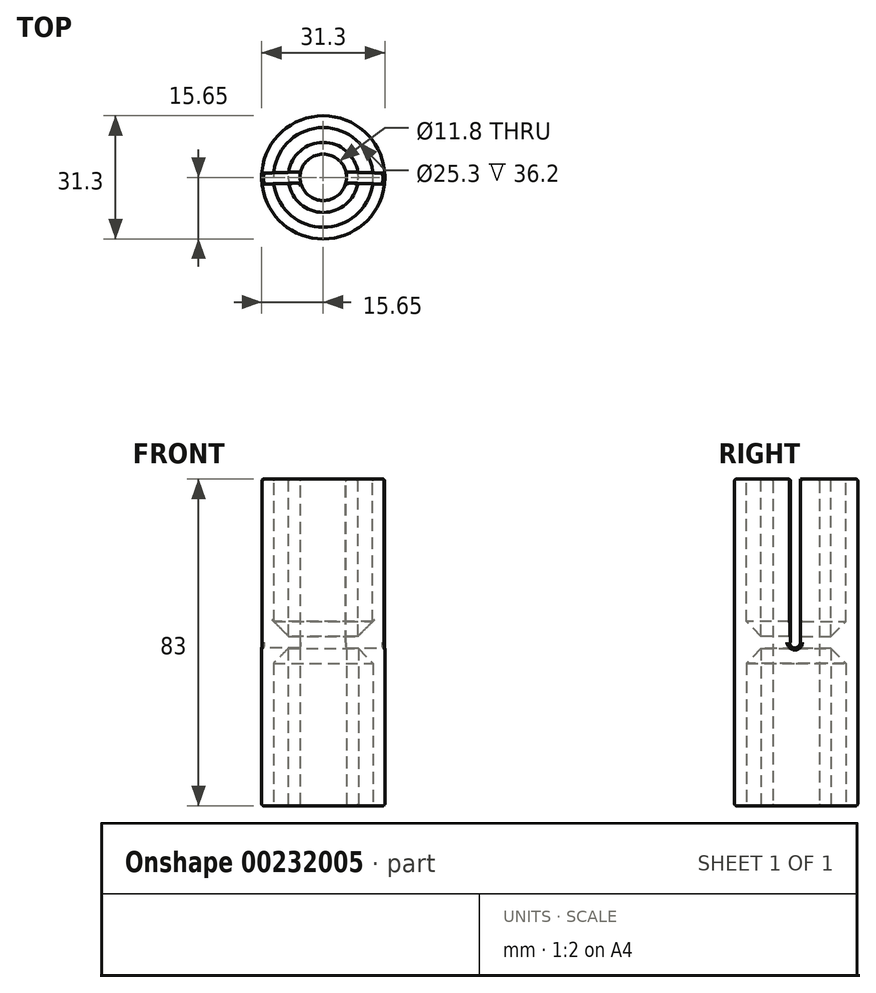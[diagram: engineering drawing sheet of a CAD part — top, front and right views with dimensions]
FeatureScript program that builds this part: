
annotation { "Feature Type Name" : "Feature", "Feature Type Description" : "" }
export const myFeature = defineFeature(function(context is Context, id is Id, definition is map)
    precondition{}
    {
        {
            var Q0;
            Q0=qCreatedBy(makeId("Top.planeOp"),FACE);
            var sketch = newSketch(context, id + "F0", { "sketchPlane" : qUnion([Q0])});
            skCircle(sketch, "E0", {"center": v(0, 0) * mm, "radius": 15.65 * mm});
            skCircle(sketch, "E1", {"center": v(0, 0) * mm, "radius": 5.9 * mm});
            skSolve(sketch);
        }
        {
            var Q0;
            Q0 = qSketchRegion(id + "F0", true);
            extrude(context, id + "F1", {"entities" : qUnion([Q0]), "endBound" : BoundingType.SYMMETRIC, "depth" : 83 * mm});
        }
        {
            var Q0;
            Q0=makeQuery(id+"F1.opExtrude","CAP_FACE",FACE,{"disambiguationData":[OSD([sQuery(id+"F0.wireOp",EDGE,"E0"),sQuery(id+"F0.wireOp",EDGE,"E1")])],"isStart":false});
            var sketch = newSketch(context, id + "F2", { "sketchPlane" : qUnion([Q0])});
            skCircle(sketch, "E2", {"center": v(0, 0) * mm, "radius": 12.65 * mm});
            skCircle(sketch, "E3", {"center": v(0, 0) * mm, "radius": 8.9 * mm});
            skSolve(sketch);
        }
        {
            var Q0;
            Q0 = qSketchRegion(id + "F2", true);
            extrude(context, id + "F3", {"entities" : qUnion([Q0]), "operationType" : NewBodyOperationType.REMOVE, "oppositeDirection" : true, "depth" : 40 * mm});
        }
        {
            var Q0;
            Q0=makeQuery(id+"F1.opExtrude","CAP_FACE",FACE,{"disambiguationData":[OSD([sQuery(id+"F0.wireOp",EDGE,"E0"),sQuery(id+"F0.wireOp",EDGE,"E1")])],"isStart":true});
            var sketch = newSketch(context, id + "F4", { "sketchPlane" : qUnion([Q0])});
            skCircle(sketch, "E4", {"center": v(0, 0) * mm, "radius": 8.9 * mm});
            skCircle(sketch, "E5", {"center": v(0, 0) * mm, "radius": 12.65 * mm});
            skSolve(sketch);
        }
        {
            var Q0;
            Q0 = qSketchRegion(id + "F4", true);
            extrude(context, id + "F5", {"entities" : qUnion([Q0]), "operationType" : NewBodyOperationType.REMOVE, "oppositeDirection" : true, "depth" : 40 * mm});
        }
        {
            var Q0;
            {var subQ0=sQuery(id+"F0.wireOp",EDGE,"E1");Q0=makeQuery(id+"F3.boolean.opBoolean","SPLIT",FACE,{"disambiguationData":[TD([makeQuery(id+"F1.opExtrude","SWEPT_FACE",FACE,{"disambiguationData":[OSD([subQ0])]})])],"derivedFrom":makeQuery(id+"F1.opExtrude","CAP_FACE",FACE,{"disambiguationData":[OSD([sQuery(id+"F0.wireOp",EDGE,"E0"),subQ0])],"isStart":false})});}
            var sketch = newSketch(context, id + "F6", { "sketchPlane" : qUnion([Q0])});
            skCircle(sketch, "E6", {"center": v(0, -340) * mm, "radius": 340 * mm, "construction": true});
            skPoint(sketch, "E7", {"position": v(0, 0) * mm});
            skSolve(sketch);
        }
        {
            var Q0;
            Q0=qCreatedBy(makeId("Right.planeOp"),FACE);
            var sketch = newSketch(context, id + "F7", { "sketchPlane" : qUnion([Q0])});
            skLineSegment(sketch, "E8", {"start": v(1.4, 41.5) * mm, "end": v(0, 41.5) * mm});
            skLineSegment(sketch, "E9", {"start": v(1.4, 41.5) * mm, "end": v(1.4, 0) * mm});
            skArc(sketch, "E10", {"start": v(0, -1.4) * mm, "mid": v(0.99, -0.99) * mm, "end": v(1.4, 0) * mm});
            skArc(sketch, "E11.MirrorCS", {"start": v(0, -1.4) * mm, "mid": v(-0.99, -0.99) * mm, "end": v(-1.4, 0) * mm});
            skLineSegment(sketch, "E12.MirrorCS", {"start": v(-1.4, 41.5) * mm, "end": v(-1.4, 0) * mm});
            skLineSegment(sketch, "E13", {"start": v(0, 41.5) * mm, "end": v(-1.4, 41.5) * mm});
            skSolve(sketch);
        }
        {
            var Q0;
            Q0=qCreatedBy(makeId("Right.planeOp"),FACE);
            var sketch = newSketch(context, id + "F8", { "sketchPlane" : qUnion([Q0])});
            skLineSegment(sketch, "E14", {"start": v(-340, -124.57) * mm, "end": v(-340, 184) * mm, "construction": true});
            skSolve(sketch);
        }
        {
            var Q0;
            Q0 = qSketchRegion(id + "F7", true);
            var Q1;
            Q1=sQuery(id+"F8.wireOp",EDGE,"E14");
            revolve(context, id + "F9", {"operationType" : NewBodyOperationType.REMOVE, "entities" : qUnion([Q0]), "axis" : qUnion([Q1]), "revolveType" : RevolveType.FULL, "oppositeDirection" : true});
        }
        {
            var Q0;
            Q0=makeQuery(id+"F5.boolean.opBoolean","COPY",EDGE,{"derivedFrom":makeQuery(id+"F5.opExtrude","CAP_EDGE",EDGE,{"disambiguationData":[OSD([sQuery(id+"F4.wireOp",EDGE,"E5")])],"isStart":false})});
            chamfer(context, id + "F10", {"entities" : qUnion([Q0]), "width" : 3.8 * mm, "tangentPropagation" : true});
        }
        {
            var Q0;
            {var subQ0=sQuery(id+"F2.wireOp",EDGE,"E2");Q0=makeQuery(id+"F9.boolean.opBoolean","SPLIT",EDGE,{"disambiguationData":[TD([makeQuery(id+"F9.opRevolve","SWEPT_FACE",FACE,{"disambiguationData":[OSD([sQuery(id+"F7.wireOp",EDGE,"E12.MirrorCS")])]})])],"derivedFrom":makeQuery(id+"F3.boolean.opBoolean","COPY",EDGE,{"derivedFrom":makeQuery(id+"F3.opExtrude","CAP_EDGE",EDGE,{"disambiguationData":[OSD([subQ0])],"isStart":false})})});}
            var Q1;
            {var subQ0=sQuery(id+"F2.wireOp",EDGE,"E2");Q1=makeQuery(id+"F9.boolean.opBoolean","SPLIT",EDGE,{"disambiguationData":[TD([makeQuery(id+"F9.opRevolve","SWEPT_FACE",FACE,{"disambiguationData":[OSD([sQuery(id+"F7.wireOp",EDGE,"E9")])]})])],"derivedFrom":makeQuery(id+"F3.boolean.opBoolean","COPY",EDGE,{"derivedFrom":makeQuery(id+"F3.opExtrude","CAP_EDGE",EDGE,{"disambiguationData":[OSD([subQ0])],"isStart":false})})});}
            chamfer(context, id + "F11", {"entities" : qUnion([Q0, Q1]), "width" : 3.8 * mm, "tangentPropagation" : true});
        }
        {
            var Q0;
            {var subQ0=sQuery(id+"F0.wireOp",EDGE,"E0");Q0=makeQuery(id+"F9.boolean.opBoolean","SPLIT",EDGE,{"disambiguationData":[TD([makeQuery(id+"F9.opRevolve","SWEPT_FACE",FACE,{"disambiguationData":[OSD([sQuery(id+"F7.wireOp",EDGE,"E9")])]})])],"derivedFrom":makeQuery(id+"F1.opExtrude","CAP_EDGE",EDGE,{"disambiguationData":[OSD([subQ0])],"isStart":false})});}
            var Q1;
            {var subQ0=sQuery(id+"F2.wireOp",EDGE,"E2");Q1=makeQuery(id+"F9.boolean.opBoolean","SPLIT",EDGE,{"disambiguationData":[TD([makeQuery(id+"F9.opRevolve","SWEPT_FACE",FACE,{"disambiguationData":[OSD([sQuery(id+"F7.wireOp",EDGE,"E9")])]})])],"derivedFrom":makeQuery(id+"F3.boolean.opBoolean","COPY",EDGE,{"derivedFrom":makeQuery(id+"F3.opExtrude","CAP_EDGE",EDGE,{"disambiguationData":[OSD([subQ0])],"isStart":true})})});}
            var Q2;
            Q2=makeQuery(id+"F9.boolean.opBoolean","INTERSECT",EDGE,{"disambiguationData":[OD(0.0)],"derivedFrom":[makeQuery(id+"F1.opExtrude","SWEPT_FACE",FACE,{"disambiguationData":[OSD([sQuery(id+"F0.wireOp",EDGE,"E0")])]}),makeQuery(id+"F9.opRevolve","SWEPT_FACE",FACE,{"disambiguationData":[OSD([sQuery(id+"F7.wireOp",EDGE,"E9")])]})]});
            var Q3;
            {var subQ0=sQuery(id+"F0.wireOp",EDGE,"E0");var subQ1=sQuery(id+"F7.wireOp",EDGE,"E9");Q3=makeQuery(id+"F9.boolean.opBoolean","COPY",EDGE,{"disambiguationData":[TD([makeQuery(id+"F1.opExtrude","SWEPT_FACE",FACE,{"disambiguationData":[OSD([subQ0])]}),makeQuery(id+"F1.opExtrude","CAP_FACE",FACE,{"disambiguationData":[OSD([subQ0,sQuery(id+"F0.wireOp",EDGE,"E1")])],"isStart":false}),makeQuery(id+"F3.boolean.opBoolean","COPY",FACE,{"derivedFrom":makeQuery(id+"F3.opExtrude","SWEPT_FACE",FACE,{"disambiguationData":[OSD([sQuery(id+"F2.wireOp",EDGE,"E2")])]})}),makeQuery(id+"F9.opRevolve","SWEPT_FACE",FACE,{"disambiguationData":[OSD([subQ1])]})]),OD(0.0)],"derivedFrom":makeQuery(id+"F9.opRevolve","SWEPT_EDGE",EDGE,{"disambiguationData":[OSD([sQuery(id+"F7.wireOp",EDGE,"E8"),subQ1])]})});}
            var Q4;
            {var subQ0=sQuery(id+"F0.wireOp",EDGE,"E0");var subQ1=sQuery(id+"F7.wireOp",EDGE,"E12.MirrorCS");Q4=makeQuery(id+"F9.boolean.opBoolean","COPY",EDGE,{"disambiguationData":[TD([makeQuery(id+"F1.opExtrude","SWEPT_FACE",FACE,{"disambiguationData":[OSD([subQ0])]}),makeQuery(id+"F1.opExtrude","CAP_FACE",FACE,{"disambiguationData":[OSD([subQ0,sQuery(id+"F0.wireOp",EDGE,"E1")])],"isStart":false}),makeQuery(id+"F3.boolean.opBoolean","COPY",FACE,{"derivedFrom":makeQuery(id+"F3.opExtrude","SWEPT_FACE",FACE,{"disambiguationData":[OSD([sQuery(id+"F2.wireOp",EDGE,"E2")])]})}),makeQuery(id+"F9.opRevolve","SWEPT_FACE",FACE,{"disambiguationData":[OSD([subQ1])]})]),OD(0.0)],"derivedFrom":makeQuery(id+"F9.opRevolve","SWEPT_EDGE",EDGE,{"disambiguationData":[OSD([subQ1,sQuery(id+"F7.wireOp",EDGE,"E13")])]})});}
            var Q5;
            {var subQ0=sQuery(id+"F0.wireOp",EDGE,"E0");Q5=makeQuery(id+"F9.boolean.opBoolean","SPLIT",EDGE,{"disambiguationData":[TD([makeQuery(id+"F9.opRevolve","SWEPT_FACE",FACE,{"disambiguationData":[OSD([sQuery(id+"F7.wireOp",EDGE,"E12.MirrorCS")])]})])],"derivedFrom":makeQuery(id+"F1.opExtrude","CAP_EDGE",EDGE,{"disambiguationData":[OSD([subQ0])],"isStart":false})});}
            var Q6;
            {var subQ0=sQuery(id+"F2.wireOp",EDGE,"E2");Q6=makeQuery(id+"F9.boolean.opBoolean","SPLIT",EDGE,{"disambiguationData":[TD([makeQuery(id+"F9.opRevolve","SWEPT_FACE",FACE,{"disambiguationData":[OSD([sQuery(id+"F7.wireOp",EDGE,"E12.MirrorCS")])]})])],"derivedFrom":makeQuery(id+"F3.boolean.opBoolean","COPY",EDGE,{"derivedFrom":makeQuery(id+"F3.opExtrude","CAP_EDGE",EDGE,{"disambiguationData":[OSD([subQ0])],"isStart":true})})});}
            var Q7;
            Q7=makeQuery(id+"F9.boolean.opBoolean","INTERSECT",EDGE,{"disambiguationData":[OD(0.0)],"derivedFrom":[makeQuery(id+"F3.boolean.opBoolean","COPY",FACE,{"derivedFrom":makeQuery(id+"F3.opExtrude","SWEPT_FACE",FACE,{"disambiguationData":[OSD([sQuery(id+"F2.wireOp",EDGE,"E2")])]})}),makeQuery(id+"F9.opRevolve","SWEPT_FACE",FACE,{"disambiguationData":[OSD([sQuery(id+"F7.wireOp",EDGE,"E9")])]})]});
            var Q8;
            Q8=makeQuery(id+"F9.boolean.opBoolean","INTERSECT",EDGE,{"disambiguationData":[OD(1.0)],"derivedFrom":[makeQuery(id+"F1.opExtrude","SWEPT_FACE",FACE,{"disambiguationData":[OSD([sQuery(id+"F0.wireOp",EDGE,"E0")])]}),makeQuery(id+"F9.opRevolve","SWEPT_FACE",FACE,{"disambiguationData":[OSD([sQuery(id+"F7.wireOp",EDGE,"E9")])]})]});
            var Q9;
            Q9=makeQuery(id+"F9.boolean.opBoolean","INTERSECT",EDGE,{"disambiguationData":[OD(1.0)],"derivedFrom":[makeQuery(id+"F3.boolean.opBoolean","COPY",FACE,{"derivedFrom":makeQuery(id+"F3.opExtrude","SWEPT_FACE",FACE,{"disambiguationData":[OSD([sQuery(id+"F2.wireOp",EDGE,"E2")])]})}),makeQuery(id+"F9.opRevolve","SWEPT_FACE",FACE,{"disambiguationData":[OSD([sQuery(id+"F7.wireOp",EDGE,"E9")])]})]});
            var Q10;
            {var subQ0=sQuery(id+"F0.wireOp",EDGE,"E0");var subQ1=sQuery(id+"F7.wireOp",EDGE,"E9");Q10=makeQuery(id+"F9.boolean.opBoolean","COPY",EDGE,{"disambiguationData":[TD([makeQuery(id+"F1.opExtrude","SWEPT_FACE",FACE,{"disambiguationData":[OSD([subQ0])]}),makeQuery(id+"F1.opExtrude","CAP_FACE",FACE,{"disambiguationData":[OSD([subQ0,sQuery(id+"F0.wireOp",EDGE,"E1")])],"isStart":false}),makeQuery(id+"F3.boolean.opBoolean","COPY",FACE,{"derivedFrom":makeQuery(id+"F3.opExtrude","SWEPT_FACE",FACE,{"disambiguationData":[OSD([sQuery(id+"F2.wireOp",EDGE,"E2")])]})}),makeQuery(id+"F9.opRevolve","SWEPT_FACE",FACE,{"disambiguationData":[OSD([subQ1])]})]),OD(1.0)],"derivedFrom":makeQuery(id+"F9.opRevolve","SWEPT_EDGE",EDGE,{"disambiguationData":[OSD([sQuery(id+"F7.wireOp",EDGE,"E8"),subQ1])]})});}
            var Q11;
            {var subQ0=sQuery(id+"F0.wireOp",EDGE,"E0");var subQ1=sQuery(id+"F7.wireOp",EDGE,"E12.MirrorCS");Q11=makeQuery(id+"F9.boolean.opBoolean","COPY",EDGE,{"disambiguationData":[TD([makeQuery(id+"F1.opExtrude","SWEPT_FACE",FACE,{"disambiguationData":[OSD([subQ0])]}),makeQuery(id+"F1.opExtrude","CAP_FACE",FACE,{"disambiguationData":[OSD([subQ0,sQuery(id+"F0.wireOp",EDGE,"E1")])],"isStart":false}),makeQuery(id+"F3.boolean.opBoolean","COPY",FACE,{"derivedFrom":makeQuery(id+"F3.opExtrude","SWEPT_FACE",FACE,{"disambiguationData":[OSD([sQuery(id+"F2.wireOp",EDGE,"E2")])]})}),makeQuery(id+"F9.opRevolve","SWEPT_FACE",FACE,{"disambiguationData":[OSD([subQ1])]})]),OD(1.0)],"derivedFrom":makeQuery(id+"F9.opRevolve","SWEPT_EDGE",EDGE,{"disambiguationData":[OSD([subQ1,sQuery(id+"F7.wireOp",EDGE,"E13")])]})});}
            var Q12;
            {var subQ0=sQuery(id+"F2.wireOp",EDGE,"E3");Q12=makeQuery(id+"F9.boolean.opBoolean","SPLIT",EDGE,{"disambiguationData":[TD([makeQuery(id+"F9.opRevolve","SWEPT_FACE",FACE,{"disambiguationData":[OSD([sQuery(id+"F7.wireOp",EDGE,"E12.MirrorCS")])]})])],"derivedFrom":makeQuery(id+"F3.boolean.opBoolean","COPY",EDGE,{"derivedFrom":makeQuery(id+"F3.opExtrude","CAP_EDGE",EDGE,{"disambiguationData":[OSD([subQ0])],"isStart":true})})});}
            var Q13;
            {var subQ0=sQuery(id+"F0.wireOp",EDGE,"E1");var subQ1=sQuery(id+"F7.wireOp",EDGE,"E12.MirrorCS");Q13=makeQuery(id+"F9.boolean.opBoolean","COPY",EDGE,{"disambiguationData":[TD([makeQuery(id+"F1.opExtrude","CAP_FACE",FACE,{"disambiguationData":[OSD([sQuery(id+"F0.wireOp",EDGE,"E0"),subQ0])],"isStart":false}),makeQuery(id+"F1.opExtrude","SWEPT_FACE",FACE,{"disambiguationData":[OSD([subQ0])]}),makeQuery(id+"F3.boolean.opBoolean","COPY",FACE,{"derivedFrom":makeQuery(id+"F3.opExtrude","SWEPT_FACE",FACE,{"disambiguationData":[OSD([sQuery(id+"F2.wireOp",EDGE,"E3")])]})}),makeQuery(id+"F9.opRevolve","SWEPT_FACE",FACE,{"disambiguationData":[OSD([subQ1])]})]),OD(1.0)],"derivedFrom":makeQuery(id+"F9.opRevolve","SWEPT_EDGE",EDGE,{"disambiguationData":[OSD([subQ1,sQuery(id+"F7.wireOp",EDGE,"E13")])]})});}
            var Q14;
            {var subQ0=sQuery(id+"F0.wireOp",EDGE,"E1");var subQ1=sQuery(id+"F7.wireOp",EDGE,"E9");Q14=makeQuery(id+"F9.boolean.opBoolean","COPY",EDGE,{"disambiguationData":[TD([makeQuery(id+"F1.opExtrude","CAP_FACE",FACE,{"disambiguationData":[OSD([sQuery(id+"F0.wireOp",EDGE,"E0"),subQ0])],"isStart":false}),makeQuery(id+"F1.opExtrude","SWEPT_FACE",FACE,{"disambiguationData":[OSD([subQ0])]}),makeQuery(id+"F3.boolean.opBoolean","COPY",FACE,{"derivedFrom":makeQuery(id+"F3.opExtrude","SWEPT_FACE",FACE,{"disambiguationData":[OSD([sQuery(id+"F2.wireOp",EDGE,"E3")])]})}),makeQuery(id+"F9.opRevolve","SWEPT_FACE",FACE,{"disambiguationData":[OSD([subQ1])]})]),OD(1.0)],"derivedFrom":makeQuery(id+"F9.opRevolve","SWEPT_EDGE",EDGE,{"disambiguationData":[OSD([sQuery(id+"F7.wireOp",EDGE,"E8"),subQ1])]})});}
            var Q15;
            {var subQ0=sQuery(id+"F2.wireOp",EDGE,"E3");Q15=makeQuery(id+"F9.boolean.opBoolean","SPLIT",EDGE,{"disambiguationData":[TD([makeQuery(id+"F9.opRevolve","SWEPT_FACE",FACE,{"disambiguationData":[OSD([sQuery(id+"F7.wireOp",EDGE,"E9")])]})])],"derivedFrom":makeQuery(id+"F3.boolean.opBoolean","COPY",EDGE,{"derivedFrom":makeQuery(id+"F3.opExtrude","CAP_EDGE",EDGE,{"disambiguationData":[OSD([subQ0])],"isStart":true})})});}
            var Q16;
            {var subQ0=sQuery(id+"F0.wireOp",EDGE,"E1");var subQ1=sQuery(id+"F7.wireOp",EDGE,"E9");Q16=makeQuery(id+"F9.boolean.opBoolean","COPY",EDGE,{"disambiguationData":[TD([makeQuery(id+"F1.opExtrude","CAP_FACE",FACE,{"disambiguationData":[OSD([sQuery(id+"F0.wireOp",EDGE,"E0"),subQ0])],"isStart":false}),makeQuery(id+"F1.opExtrude","SWEPT_FACE",FACE,{"disambiguationData":[OSD([subQ0])]}),makeQuery(id+"F3.boolean.opBoolean","COPY",FACE,{"derivedFrom":makeQuery(id+"F3.opExtrude","SWEPT_FACE",FACE,{"disambiguationData":[OSD([sQuery(id+"F2.wireOp",EDGE,"E3")])]})}),makeQuery(id+"F9.opRevolve","SWEPT_FACE",FACE,{"disambiguationData":[OSD([subQ1])]})]),OD(0.0)],"derivedFrom":makeQuery(id+"F9.opRevolve","SWEPT_EDGE",EDGE,{"disambiguationData":[OSD([sQuery(id+"F7.wireOp",EDGE,"E8"),subQ1])]})});}
            var Q17;
            {var subQ0=sQuery(id+"F0.wireOp",EDGE,"E1");var subQ1=sQuery(id+"F7.wireOp",EDGE,"E12.MirrorCS");Q17=makeQuery(id+"F9.boolean.opBoolean","COPY",EDGE,{"disambiguationData":[TD([makeQuery(id+"F1.opExtrude","CAP_FACE",FACE,{"disambiguationData":[OSD([sQuery(id+"F0.wireOp",EDGE,"E0"),subQ0])],"isStart":false}),makeQuery(id+"F1.opExtrude","SWEPT_FACE",FACE,{"disambiguationData":[OSD([subQ0])]}),makeQuery(id+"F3.boolean.opBoolean","COPY",FACE,{"derivedFrom":makeQuery(id+"F3.opExtrude","SWEPT_FACE",FACE,{"disambiguationData":[OSD([sQuery(id+"F2.wireOp",EDGE,"E3")])]})}),makeQuery(id+"F9.opRevolve","SWEPT_FACE",FACE,{"disambiguationData":[OSD([subQ1])]})]),OD(0.0)],"derivedFrom":makeQuery(id+"F9.opRevolve","SWEPT_EDGE",EDGE,{"disambiguationData":[OSD([subQ1,sQuery(id+"F7.wireOp",EDGE,"E13")])]})});}
            var Q18;
            {var subQ0=sQuery(id+"F0.wireOp",EDGE,"E1");Q18=makeQuery(id+"F9.boolean.opBoolean","SPLIT",EDGE,{"disambiguationData":[TD([makeQuery(id+"F9.opRevolve","SWEPT_FACE",FACE,{"disambiguationData":[OSD([sQuery(id+"F7.wireOp",EDGE,"E12.MirrorCS")])]})])],"derivedFrom":makeQuery(id+"F1.opExtrude","CAP_EDGE",EDGE,{"disambiguationData":[OSD([subQ0])],"isStart":false})});}
            var Q19;
            {var subQ0=sQuery(id+"F0.wireOp",EDGE,"E1");Q19=makeQuery(id+"F9.boolean.opBoolean","SPLIT",EDGE,{"disambiguationData":[TD([makeQuery(id+"F9.opRevolve","SWEPT_FACE",FACE,{"disambiguationData":[OSD([sQuery(id+"F7.wireOp",EDGE,"E9")])]})])],"derivedFrom":makeQuery(id+"F1.opExtrude","CAP_EDGE",EDGE,{"disambiguationData":[OSD([subQ0])],"isStart":false})});}
            var Q20;
            Q20=makeQuery(id+"F1.opExtrude","CAP_EDGE",EDGE,{"disambiguationData":[OSD([sQuery(id+"F0.wireOp",EDGE,"E0")])],"isStart":true});
            var Q21;
            Q21=makeQuery(id+"F5.boolean.opBoolean","COPY",EDGE,{"derivedFrom":makeQuery(id+"F5.opExtrude","CAP_EDGE",EDGE,{"disambiguationData":[OSD([sQuery(id+"F4.wireOp",EDGE,"E5")])],"isStart":true})});
            var Q22;
            Q22=makeQuery(id+"F5.boolean.opBoolean","COPY",EDGE,{"derivedFrom":makeQuery(id+"F5.opExtrude","CAP_EDGE",EDGE,{"disambiguationData":[OSD([sQuery(id+"F4.wireOp",EDGE,"E4")])],"isStart":true})});
            var Q23;
            Q23=makeQuery(id+"F1.opExtrude","CAP_EDGE",EDGE,{"disambiguationData":[OSD([sQuery(id+"F0.wireOp",EDGE,"E1")])],"isStart":true});
            fillet(context, id + "F12", {"entities" : qUnion([Q0, Q1, Q2, Q3, Q4, Q5, Q6, Q7, Q8, Q9, Q10, Q11, Q12, Q13, Q14, Q15, Q16, Q17, Q18, Q19, Q20, Q21, Q22, Q23]), "radius" : 0.5 * mm, "tangentPropagation" : true, "allowEdgeOverflow" : false});
        }
    });
